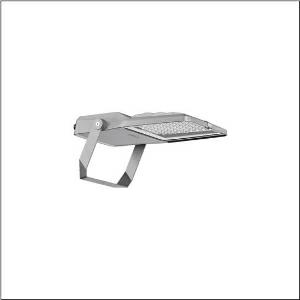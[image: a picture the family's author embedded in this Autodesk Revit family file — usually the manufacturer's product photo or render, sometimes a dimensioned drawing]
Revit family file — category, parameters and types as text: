
# Revit family: floodlight_fl_21_iq_mini___pl61_5xa7771c2c1a_d716
name_source: partatom
category: Lighting Fixtures
units: mm (PartAtom-declared; Revit-internal decimal feet)

## family parameters
Cut with Voids When Loaded = No
Host = Face
Light Source = No
Part Type = Normal
Room Calculation Point = No
Round Connector Dimension = Use Diameter
Shared = No

## types (1)
- --- (1 x LED, 11980 lm, 87.2 W, 3000K)
    Apparent Load = 87 VA
    CIE Flux Codes = 33 65 98 100 100
    Color Rendering = 70
    Color Temperature = 3000K
    Default Elevation = 1800 mm
    Description = Floodlight FL 21 iQ mini, floodlight, primary light control with lens, of PMMA, primary optical cover: protective disc, of toughened safety glass, transparent, light distribution: PL61, light emission: direct distribution, installation type: surface-mounted, LED, High Power LED, rated luminous flux: 11.980lm, luminous efficacy: 137lm/W, light colour: 730, colour temperature: 3000K, control gear: iQ Comfort/DALI, control: Auto-Match, Temp-Guard, Lumen-Switch, Night-Set, Smart-Wire, Light-Fading, Desk-Remote (wireless, voltage-free reading and setting of iQ features in the workshop via application-optimized NFC function/RFID function), optimised constant luminous flux control (CLO 2.0), with terminal, 6-pole, mains connection: 220..240V, AC, 50/60Hz, start of lifetime: 87W, end of service life: 92W, reduction: 40W, luminaire housing, of diecast aluminium, powder-coated, Siteco® metallic grey (DB 702S), corrosivity category C5 mid according to DIN EN ISO 12944, suitable for swimming pools, chlorine-resistant, sealing non-destructively replaceable, mounting bracket, of steel, galvanised, powder-coated, Siteco® metallic grey (DB 702S), protection rating (complete): IP66, insulation class (complete): insulation class II (safety insulation), certification: CE, ENEC, VDE, protection symbol: D, impact resistance: IK08, permissible operating ambient temperature: -40..+40°C, permissible operating ambient temperature for outdoor applications: -40..+50°C, standard: DIN EN 12944, LABS conformity tested according to VDMA 24364:2018-05, packaging unit: 1 piece

Light Distribution: PL61
    Height = 70 mm
    Lamp = 1 x LED
    Lamp Light Flux = 11980 lm
    Lamp Power = 87.2 W
    Lamp count = 1
    Length = 485 mm
    Luminous efficacy = 137 lm/W
    Manufacturer = Siteco
    ModVariant = No
    Model = 5XA7771C2C1A
    Number of Poles = 1
    OnlyDefault = Yes
    Power Factor = 1
    Product Name = Floodlight FL 21 iQ mini | PL61
    Product group = floodlight | pylon annexe
    ProductGroupID = 6200
    Protection Class = Protection class II
    Protection Degree = IP 66
    RLX_Detail_Level = 1
    RLX_Emergency_Light_Flux = 0 lm
    RLX_Emergency_Type = 0
    RLX_Emergency_Type_DB = No
    RlxData = <blob elided: 96441 chars, md5=f72e50a0>
    Socket = socket
    Standby Power = 0 W
    System Light Flux = 11980 lm
    System Power = 87 W
    Type Comments = factory setting: luminous flux: 100 % | dim-lin: 254 | 456 mA
    Type Image = l_1006845.jpg
    URL = http://relux.com
    VarID = @adj_173368
    Voltage = 0 V
    Weight = 0.00 kg
    Width = 337 mm

## geometry (parser evidence)
native form markers: Blend x4, Sweep x12
no freeform markers — native parametric forms only
